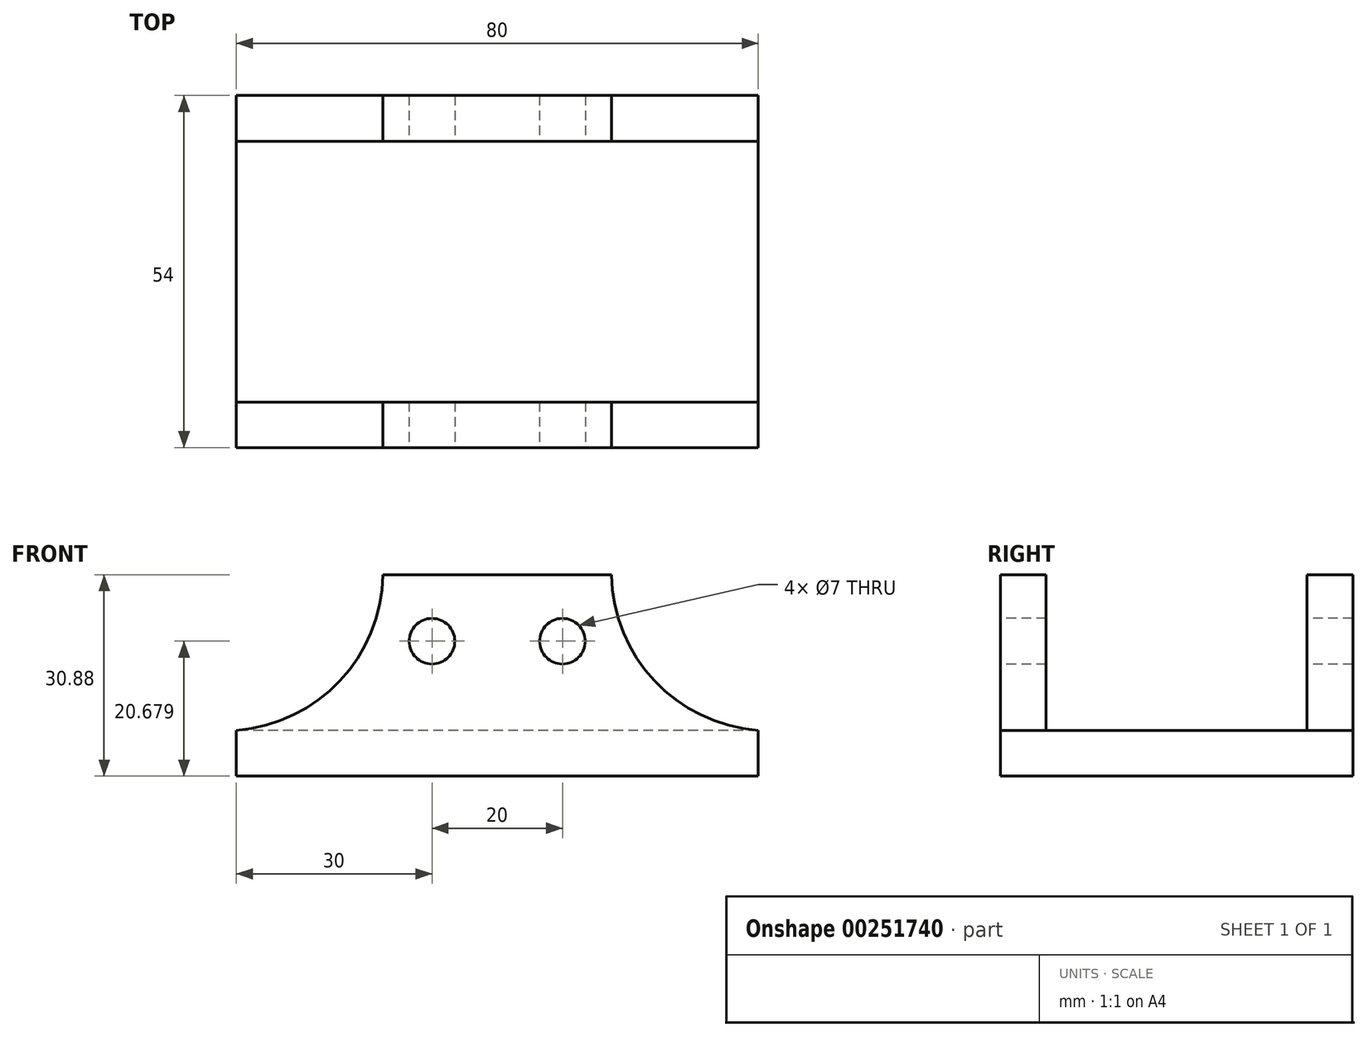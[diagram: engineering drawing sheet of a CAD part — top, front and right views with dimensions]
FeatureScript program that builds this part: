
annotation { "Feature Type Name" : "Feature", "Feature Type Description" : "" }
export const myFeature = defineFeature(function(context is Context, id is Id, definition is map)
    precondition{}
    {
        {
            var Q0;
            Q0=qCreatedBy(makeId("Top.planeOp"),FACE);
            var sketch = newSketch(context, id + "F0", { "sketchPlane" : qUnion([Q0])});
            skLineSegment(sketch, "E0.bottom", {"start": v(40, -27) * mm, "end": v(-40, -27) * mm});
            skLineSegment(sketch, "E0.top", {"start": v(40, 27) * mm, "end": v(-40, 27) * mm});
            skLineSegment(sketch, "E0.left", {"start": v(40, -27) * mm, "end": v(40, 27) * mm});
            skLineSegment(sketch, "E0.right", {"start": v(-40, -27) * mm, "end": v(-40, 27) * mm});
            skPoint(sketch, "E0.middle", {"position": v(0, 0) * mm});
            skSolve(sketch);
        }
        {
            var Q0;
            Q0 = qSketchRegion(id + "F0", true);
            extrude(context, id + "F1", {"entities" : qUnion([Q0]), "depth" : 7 * mm});
        }
        {
            var Q0;
            Q0=makeQuery(id+"F1.opExtrude","SWEPT_FACE",FACE,{"disambiguationData":[OSD([sQuery(id+"F0.wireOp",EDGE,"E0.bottom")])]});
            var sketch = newSketch(context, id + "F2", { "sketchPlane" : qUnion([Q0])});
            skLineSegment(sketch, "E1", {"start": v(-17.5, 30.88) * mm, "end": v(17.5, 30.88) * mm});
            skArc(sketch, "E2", {"start": v(-40, 7) * mm, "mid": v(-24.14, 14.6) * mm, "end": v(-17.5, 30.88) * mm});
            skPoint(sketch, "E2.first.point", {"position": v(-40, 7) * mm});
            skPoint(sketch, "E2.third.point", {"position": v(-66.29, 30.88) * mm});
            skArc(sketch, "E3", {"start": v(17.5, 30.88) * mm, "mid": v(24.14, 14.6) * mm, "end": v(40, 7) * mm});
            skPoint(sketch, "E3.first.point", {"position": v(40, 7) * mm});
            skPoint(sketch, "E3.third.point", {"position": v(47.02, 55.18) * mm});
            skLineSegment(sketch, "E4", {"start": v(-40, 7) * mm, "end": v(40, 7) * mm});
            skSolve(sketch);
        }
        {
            var Q0;
            Q0 = qSketchRegion(id + "F2", true);
            extrude(context, id + "F3", {"entities" : qUnion([Q0]), "operationType" : NewBodyOperationType.ADD, "oppositeDirection" : true, "depth" : 7 * mm, "offsetDistance" : 25 * mm});
        }
        {
            var Q0;
            Q0=makeQuery(id+"F1.opExtrude","SWEPT_BODY",BODY,{"disambiguationData":[OSD([sQuery(id+"F0.wireOp",EDGE,"E0.bottom"),sQuery(id+"F0.wireOp",EDGE,"E0.top"),sQuery(id+"F0.wireOp",EDGE,"E0.left"),sQuery(id+"F0.wireOp",EDGE,"E0.right")])]});
            var Q1;
            Q1=qCreatedBy(makeId("Front.planeOp"),FACE);
            mirror(context, id + "F4", {"operationType" : NewBodyOperationType.ADD, "entities" : qUnion([Q0]), "mirrorPlane" : qUnion([Q1])});
        }
        {
            var Q0;
            Q0=makeQuery(id+"F3.boolean.opBoolean","MERGE",FACE,{"derivedFrom":[makeQuery(id+"F1.opExtrude","SWEPT_FACE",FACE,{"disambiguationData":[OSD([sQuery(id+"F0.wireOp",EDGE,"E0.bottom")])]}),makeQuery(id+"F3.opExtrude","CAP_FACE",FACE,{"disambiguationData":[OSD([sQuery(id+"F2.wireOp",EDGE,"E1"),sQuery(id+"F2.wireOp",EDGE,"E2"),sQuery(id+"F2.wireOp",EDGE,"E3"),sQuery(id+"F2.wireOp",EDGE,"E4")])],"isStart":true})]});
            var sketch = newSketch(context, id + "F5", { "sketchPlane" : qUnion([Q0])});
            skCircle(sketch, "E5", {"center": v(-10, 20.68) * mm, "radius": 3.5 * mm});
            skCircle(sketch, "E6", {"center": v(10, 20.68) * mm, "radius": 3.5 * mm});
            skSolve(sketch);
        }
        {
            var Q0;
            Q0 = qSketchRegion(id + "F5", true);
            extrude(context, id + "F6", {"entities" : qUnion([Q0]), "operationType" : NewBodyOperationType.REMOVE, "endBound" : BoundingType.THROUGH_ALL, "oppositeDirection" : true, "depth" : 25 * mm});
        }
    });
